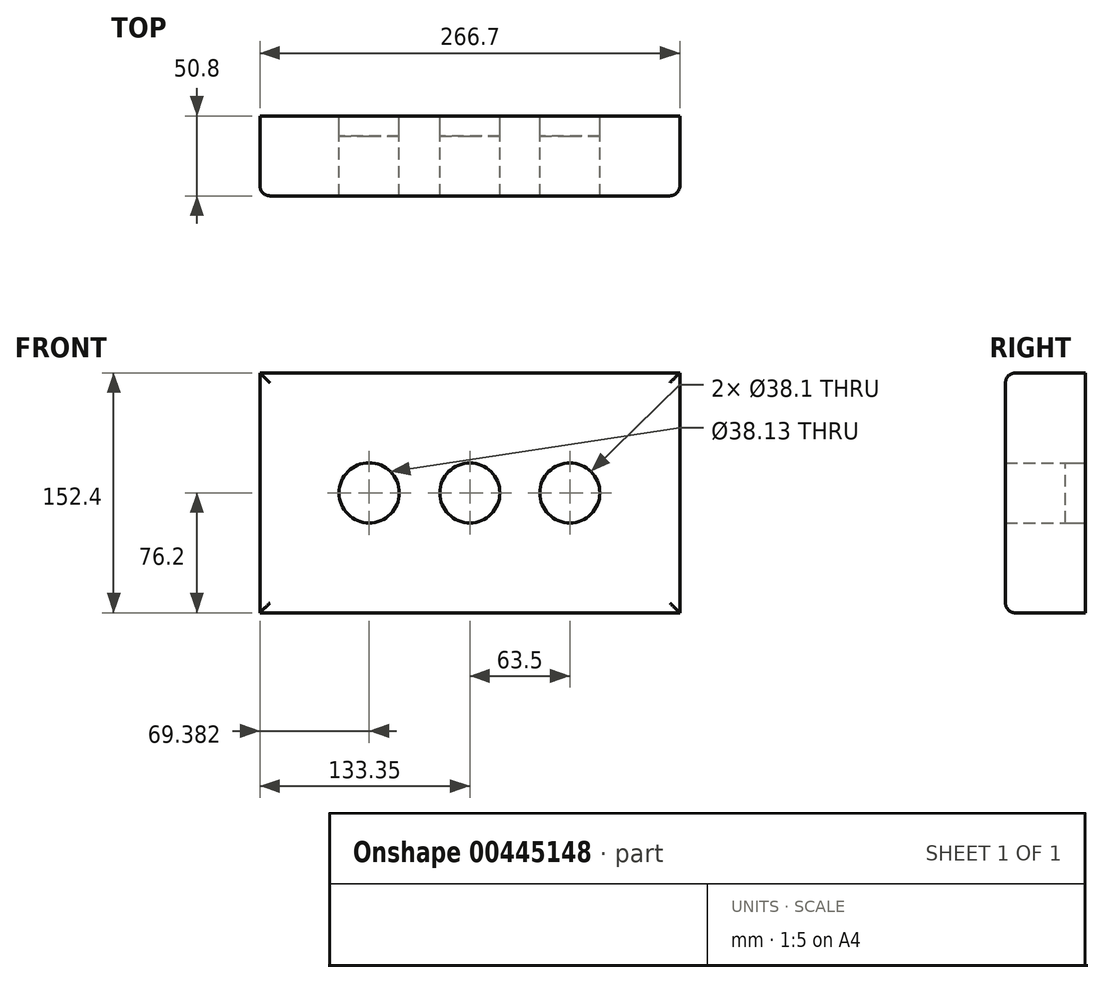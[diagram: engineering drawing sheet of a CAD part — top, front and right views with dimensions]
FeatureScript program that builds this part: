
annotation { "Feature Type Name" : "Feature", "Feature Type Description" : "" }
export const myFeature = defineFeature(function(context is Context, id is Id, definition is map)
    precondition{}
    {
        {
            var Q0;
            Q0=qCreatedBy(makeId("Front.planeOp"),FACE);
            var sketch = newSketch(context, id + "F0", { "sketchPlane" : qUnion([Q0])});
            skLineSegment(sketch, "E0.bottom", {"start": v(133.35, 76.2) * mm, "end": v(-133.35, 76.2) * mm});
            skLineSegment(sketch, "E0.top", {"start": v(133.35, -76.2) * mm, "end": v(-133.35, -76.2) * mm});
            skLineSegment(sketch, "E0.left", {"start": v(133.35, 76.2) * mm, "end": v(133.35, -76.2) * mm});
            skLineSegment(sketch, "E0.right", {"start": v(-133.35, 76.2) * mm, "end": v(-133.35, -76.2) * mm});
            skPoint(sketch, "E0.middle", {"position": v(0, 0) * mm});
            skCircle(sketch, "E1", {"center": v(0, 0) * mm, "radius": 19.05 * mm});
            skLineSegment(sketch, "E2", {"start": v(-19.05, 0) * mm, "end": v(-44.45, 0) * mm});
            skLineSegment(sketch, "E3", {"start": v(19.05, 0) * mm, "end": v(44.45, 0) * mm});
            skCircle(sketch, "E4", {"center": v(-63.97, 0) * mm, "radius": 19.06 * mm});
            skCircle(sketch, "E5", {"center": v(63.5, 0) * mm, "radius": 19.05 * mm});
            skSolve(sketch);
        }
        {
            var Q0;
            Q0=makeQuery(id+"F0.imprint","IMPRINT",FACE,{"disambiguationData":[TD([[makeQuery(id+"F0.imprint","IMPRINT",EDGE,{"derivedFrom":sQuery(id+"F0.wireOp",EDGE,"E0.bottom")}),1.0]])]});
            extrude(context, id + "F1", {"entities" : qUnion([Q0]), "depth" : 50.8 * mm});
        }
        {
            var Q0;
            Q0=makeQuery(id+"F0.imprint","IMPRINT",FACE,{"disambiguationData":[TD([[makeQuery(id+"F0.imprint","IMPRINT",EDGE,{"derivedFrom":sQuery(id+"F0.wireOp",EDGE,"E4")}),1.0]])]});
            var Q1;
            {var subQ0=sQuery(id+"F0.wireOp",EDGE,"E1");var subQ1=makeQuery(id+"F0.imprint","IMPRINT",VERTEX,{"disambiguationData":[OD(0.0)],"derivedFrom":subQ0});Q1=makeQuery(id+"F0.imprint","IMPRINT",FACE,{"disambiguationData":[TD([[makeQuery(id+"F0.imprint","IMPRINT",EDGE,{"disambiguationData":[TD([[subQ1,1.0]])],"derivedFrom":subQ0}),1.0]])]});}
            var Q2;
            Q2=makeQuery(id+"F0.imprint","IMPRINT",FACE,{"disambiguationData":[TD([[makeQuery(id+"F0.imprint","IMPRINT",EDGE,{"derivedFrom":sQuery(id+"F0.wireOp",EDGE,"E5")}),1.0]])]});
            extrude(context, id + "F2", {"entities" : qUnion([Q0, Q1, Q2]), "depth" : 12.7 * mm});
        }
        {
            var Q0;
            Q0=makeQuery(id+"F1.opExtrude","CAP_EDGE",EDGE,{"disambiguationData":[OSD([sQuery(id+"F0.wireOp",EDGE,"E0.bottom")])],"isStart":false});
            var Q1;
            Q1=makeQuery(id+"F1.opExtrude","CAP_EDGE",EDGE,{"disambiguationData":[OSD([sQuery(id+"F0.wireOp",EDGE,"E0.right")])],"isStart":false});
            var Q2;
            Q2=makeQuery(id+"F1.opExtrude","CAP_EDGE",EDGE,{"disambiguationData":[OSD([sQuery(id+"F0.wireOp",EDGE,"E0.left")])],"isStart":false});
            var Q3;
            Q3=makeQuery(id+"F1.opExtrude","CAP_EDGE",EDGE,{"disambiguationData":[OSD([sQuery(id+"F0.wireOp",EDGE,"E0.top")])],"isStart":false});
            fillet(context, id + "F3", {"entities" : qUnion([Q0, Q1, Q2, Q3]), "radius" : 6.35 * mm, "tangentPropagation" : true, "allowEdgeOverflow" : false});
        }
    });
